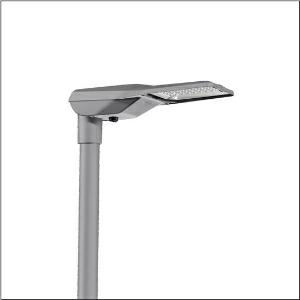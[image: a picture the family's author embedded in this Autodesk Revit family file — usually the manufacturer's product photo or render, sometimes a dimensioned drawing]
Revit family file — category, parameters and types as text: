
# Revit family: streetlight_sl_21_mini___st1_0ab_5xe2m33r08jb_ae43
name_source: partatom
category: Lighting Fixtures
units: mm (PartAtom-declared; Revit-internal decimal feet)

## family parameters
Cut with Voids When Loaded = No
Host = Face
Light Source = No
Part Type = Normal
Room Calculation Point = No
Round Connector Dimension = Use Diameter
Shared = No

## types (1)
- --- (1 x LED, 11290 lm, 87.3 W, 3000K)
    Apparent Load = 87 VA
    CIE Flux Codes = 40 74 97 100 100
    Color Rendering = 70
    Color Temperature = 3000K
    Default Elevation = 1800 mm
    Description = Streetlight SL 21 mini, mast luminaire, primary light control with lens, of PMMA, primary optical cover: cover, of toughened safety glass, transparent, light distribution: ST1.0aB, light emission: direct distribution, primary light characteristic: asymmetric, installation type: side-entry, post-top, LED, High Power LED, rated luminous flux: 11.290lm, luminous efficacy: 129lm/W, light colour: 730, colour temperature: 3000K, control: flexible luminous flux parameterisation, time-dependent luminous flux control, constant luminous flux control, overheat protection, presetting dimming logarithmic, mains connection: 220..240V, AC, 50/60Hz, start of lifetime: 87W, end of service life: 90W, reduction: 40W, luminaire housing, of diecast aluminium, powder-coated, Siteco® metallic grey (DB 702S), corrosivity category C5 mid according to DIN EN ISO 12944, please order mast flange separately, inclination adjustable: 0°, 5°, 10°, 15°, sealing non-destructively replaceable, multi-level sealing system, length: 628mm, width: 235mm, height: 110mm, mast flange for spigot size: 42mm (side-entry): 5XC10008XM4, 60/48mm (side-entry/post-top): 5XC10108XM2, 76/60mm (side-entry/post-top): 5XC10108XM1, Smart Interface below, protection rating (complete): IP66, insulation class (complete): insulation class II (safety insulation), certification: CE, ENEC, ENEC+, VDE, impact resistance: IK09, permissible operating ambient temperature for outdoor applications: -40..+50°C, standard-compliant lighting for roads and squares, packaging unit: 1 piece

Light Distribution: ST1.0aB
    Height = 110 mm
    Lamp = 1 x LED
    Lamp Light Flux = 11290 lm
    Lamp Power = 87.3 W
    Lamp count = 1
    Length = 625 mm
    Luminous efficacy = 129 lm/W
    Manufacturer = Siteco
    ModVariant = No
    Model = 5XE2M33R08JB
    Number of Poles = 1
    OnlyDefault = Yes
    Power Factor = 1
    Product Name = Streetlight SL 21 mini | ST1.0aB
    Product group = mast luminaire | pylon top
    ProductGroupID = 6100
    Protection Class = Protection class II
    Protection Degree = IP 66
    RLX_Detail_Level = 1
    RLX_Emergency_Light_Flux = 0 lm
    RLX_Emergency_Type = 0
    RLX_Emergency_Type_DB = No
    RlxData = <blob elided: 92301 chars, md5=338adf16>
    Socket = socket
    Standby Power = 0 W
    System Light Flux = 11290 lm
    System Power = 87 W
    Type Comments = factory setting: luminous flux: 100 % | dim-lin: 254 | 915 mA
    Type Image = l_1003516.jpg
    URL = http://relux.com
    VarID = @adj_100731
    Voltage = 0 V
    Weight = 0.00 kg
    Width = 234 mm

## geometry (parser evidence)
native form markers: Blend x4, Sweep x10
no freeform markers — native parametric forms only
